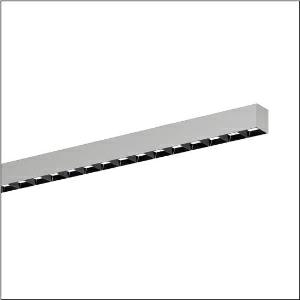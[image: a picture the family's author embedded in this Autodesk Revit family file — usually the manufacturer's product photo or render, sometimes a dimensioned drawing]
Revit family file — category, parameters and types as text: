
# Revit family: silica_r__21_51mx24dc4asb_83d0
name_source: partatom
category: Lighting Fixtures
units: mm (PartAtom-declared; Revit-internal decimal feet)

## family parameters
Cut with Voids When Loaded = No
Host = Face
Light Source = No
Part Type = Normal
Room Calculation Point = No
Round Connector Dimension = Use Diameter
Shared = No

## types (1)
- --- (1 x LED, 10800 lm, 73.7 W, 4000K)
    Apparent Load = 74 VA
    CIE Flux Codes = 74 94 99 100 100
    Color Rendering = 80
    Color Temperature = 4000K
    Default Elevation = 1800 mm
    Description = Silica® 21, office luminaire, primary light control with darklight reflector, of PMMA, black, CAT 2 (L<= 3000cd/m²), light emission: direct distribution, primary light characteristic: asymmetric, installation type: surface-mounted, LED, rated luminous flux: 10.800lm, luminous efficacy: 147lm/W, light colour: 840, colour temperature: 4000K, with terminal, 3+2-pole, max. 2.5mm², mains connection: 220..240V, AC, 50/60Hz, rated input power: 73.7W, luminaire housing, of aluminium, metallic grey (RAL 9006), length: 3.004mm, width: 53mm, height: 53mm, protection rating (complete): IP20, insulation class (complete): insulation class I (protective earthing), certification: CE, permissible operating ambient temperature: 0..+35°C, standard: EN 50419, packaging unit: 1 piece
    Height = 0 mm  [stored 0 ft]
    Lamp = 1 x LED
    Lamp Light Flux = 10800 lm
    Lamp Power = 73.7 W
    Lamp count = 1
    Length = 3004 mm
    Luminous efficacy = 147 lm/W
    Manufacturer = Siteco
    ModVariant = No
    Model = 51MX24DC4ASB
    Mounting Place = Ceiling
    Mounting Type = Recessed
    Number of Poles = 1
    OnlyDefault = Yes
    Power Factor = 1
    Product Name = Silica® 21
    Product group = office luminaire | ceiling recessed
    ProductGroupID = 401
    Protection Class = Protection class I
    Protection Degree = IP 20
    RLX_Detail_Level = 1
    RLX_Emergency_Light_Flux = 0 lm
    RLX_Emergency_Type = 0
    RLX_Emergency_Type_DB = No
    RlxData = <blob elided: 63453 chars, md5=f7130746>
    Socket = socket
    Standby Power = 0 W
    System Light Flux = 10800 lm
    System Power = 74 W
    Type Comments = factory setting: luminous flux: 100 % | dim-lin: 254 | 418 mA
    Type Image = l_1313585.jpg
    URL = http://relux.com
    VarID = @adj_071467
    Voltage = 0 V
    Weight = 0.00 kg
    Width = 53 mm

note: [stored X ft] marks values corroborated as IEEE doubles in the binary element streams (Revit-internal decimal feet)

## geometry (parser evidence)
native form markers: Blend x4, Sweep x9
no freeform markers — native parametric forms only
